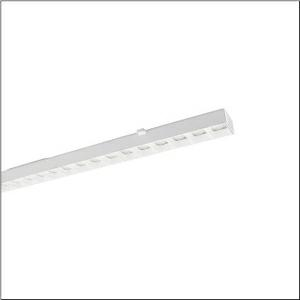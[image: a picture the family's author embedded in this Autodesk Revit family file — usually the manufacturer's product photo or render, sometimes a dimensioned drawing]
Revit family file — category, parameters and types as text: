
# Revit family: silica_r__31_fur_modario_r__31_51ry1tmb46c_60a4
name_source: partatom
category: Lighting Fixtures
units: mm (PartAtom-declared; Revit-internal decimal feet)

## family parameters
Cut with Voids When Loaded = No
Host = Face
Light Source = No
Part Type = Normal
Room Calculation Point = No
Round Connector Dimension = Use Diameter
Shared = No

## types (1)
- --- (1 x LED, 6710 lm, 37.8 W, 4000K)
    Apparent Load = 38 VA
    CIE Flux Codes = 84 98 100 100 100
    Color Rendering = 80
    Color Temperature = 4000K
    Default Elevation = 1800 mm
    Description = Silica® 31 for Modario® 31, luminaire insert, of aluminium, coated, traffic white (RAL 9016), length: 1.495mm, width: 79mm, height: 62mm, 5x system unit, system units: 299mm, LED rated luminous flux: 6.710lm, light colour: 840, control gear: ON/OFF Multilumen, with system connector: socket, mains connection: 220..240V, AC, 50/60Hz, rated input power: 38W, luminous flux adjustable on luminaire in four steps (3920/4730/5690/6710lm), connected load according to luminous flux setting (21.7/26.2/31.8/37.8W), primary light control with lens, of PMMA, primary anti-glare with reflector, of PC, CAT 2 (L<= 3000cd/m²), light emission: direct distribution, primary light characteristic: symmetric, protection rating (complete): IP20, insulation class (complete): insulation class I (protective earthing), certification: CE, UKCA, impact resistance: IK02, permissible ambient temperature for indoor applications: -20..+40°C, packaging unit: 1 piece
    Height = 62 mm  [stored 0.203412 ft]
    Lamp = 1 x LED
    Lamp Light Flux = 6710 lm
    Lamp Power = 37.8 W
    Lamp count = 1
    Length = 1495 mm
    Luminous efficacy = 178 lm/W
    Manufacturer = Siteco
    ModVariant = No
    Model = 51RY1TMB46C
    Mounting Place = Ceiling
    Mounting Type = Pendant
    Number of Poles = 1
    OnlyDefault = Yes
    Power Factor = 1
    Product Name = Silica® 31 für Modario® 31
    Product group = luminaire insert
    ProductGroupID = 902
    Protection Class = Protection class I
    Protection Degree = IP 20
    RLX_Detail_Level = 1
    RLX_Emergency_Light_Flux = 0 lm
    RLX_Emergency_Type = 0
    RLX_Emergency_Type_DB = No
    RlxData = <blob elided: 14033 chars, md5=d586ca37>
    Socket = socket
    Standby Power = 0 W
    System Light Flux = 6710 lm
    System Power = 38 W
    Type Comments = factory setting: luminous flux: 100 % | (OFF | OFF | OFF) | 350 mA
    Type Image = l_1299352.jpg
    URL = http://relux.com
    VarID = @adj_058210
    Voltage = 0 V
    Weight = 0.00 kg
    Width = 79 mm

note: [stored X ft] marks values corroborated as IEEE doubles in the binary element streams (Revit-internal decimal feet)

## geometry (parser evidence)
native form markers: Sweep x12
no freeform markers — native parametric forms only
